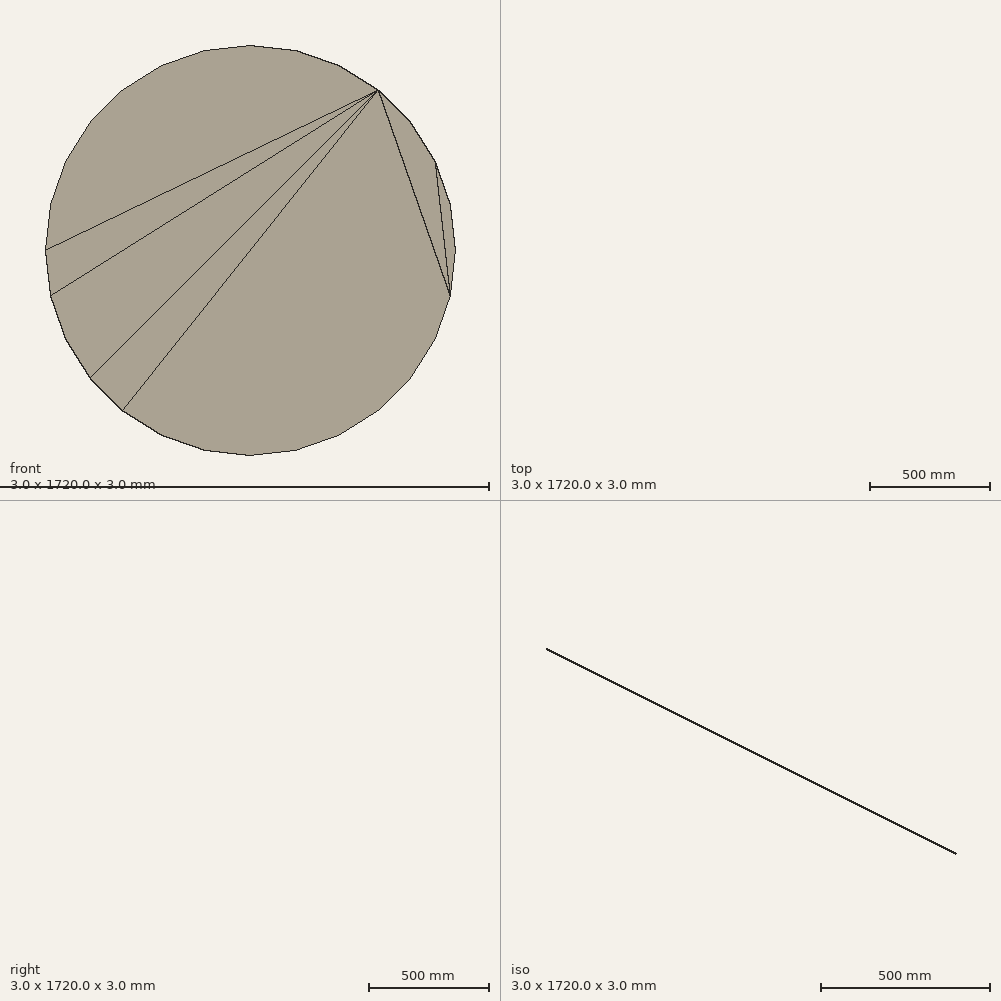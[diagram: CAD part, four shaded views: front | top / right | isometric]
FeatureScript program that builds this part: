
annotation { "Feature Type Name" : "Feature", "Feature Type Description" : "" }
export const myFeature = defineFeature(function(context is Context, id is Id, definition is map)
    precondition{}
    {
        {
            var Q0;
            Q0=qCreatedBy(makeId("Front.planeOp"),FACE);
            var sketch = newSketch(context, id + "F0", { "sketchPlane" : qUnion([Q0])});
            skCircle(sketch, "E0", {"center": v(0, 0) * mm, "radius": 1.5 * mm});
            skSolve(sketch);
        }
        {
            var Q0;
            Q0=makeQuery(id+"F0.imprint","IMPRINT",FACE,{"disambiguationData":[TD([[makeQuery(id+"F0.imprint","IMPRINT",EDGE,{"derivedFrom":sQuery(id+"F0.wireOp",EDGE,"E0")}),1.0]])]});
            extrude(context, id + "F1", {"entities" : qUnion([Q0]), "depth" : 1720 * mm, "offsetDistance" : 25 * mm});
        }
    });
